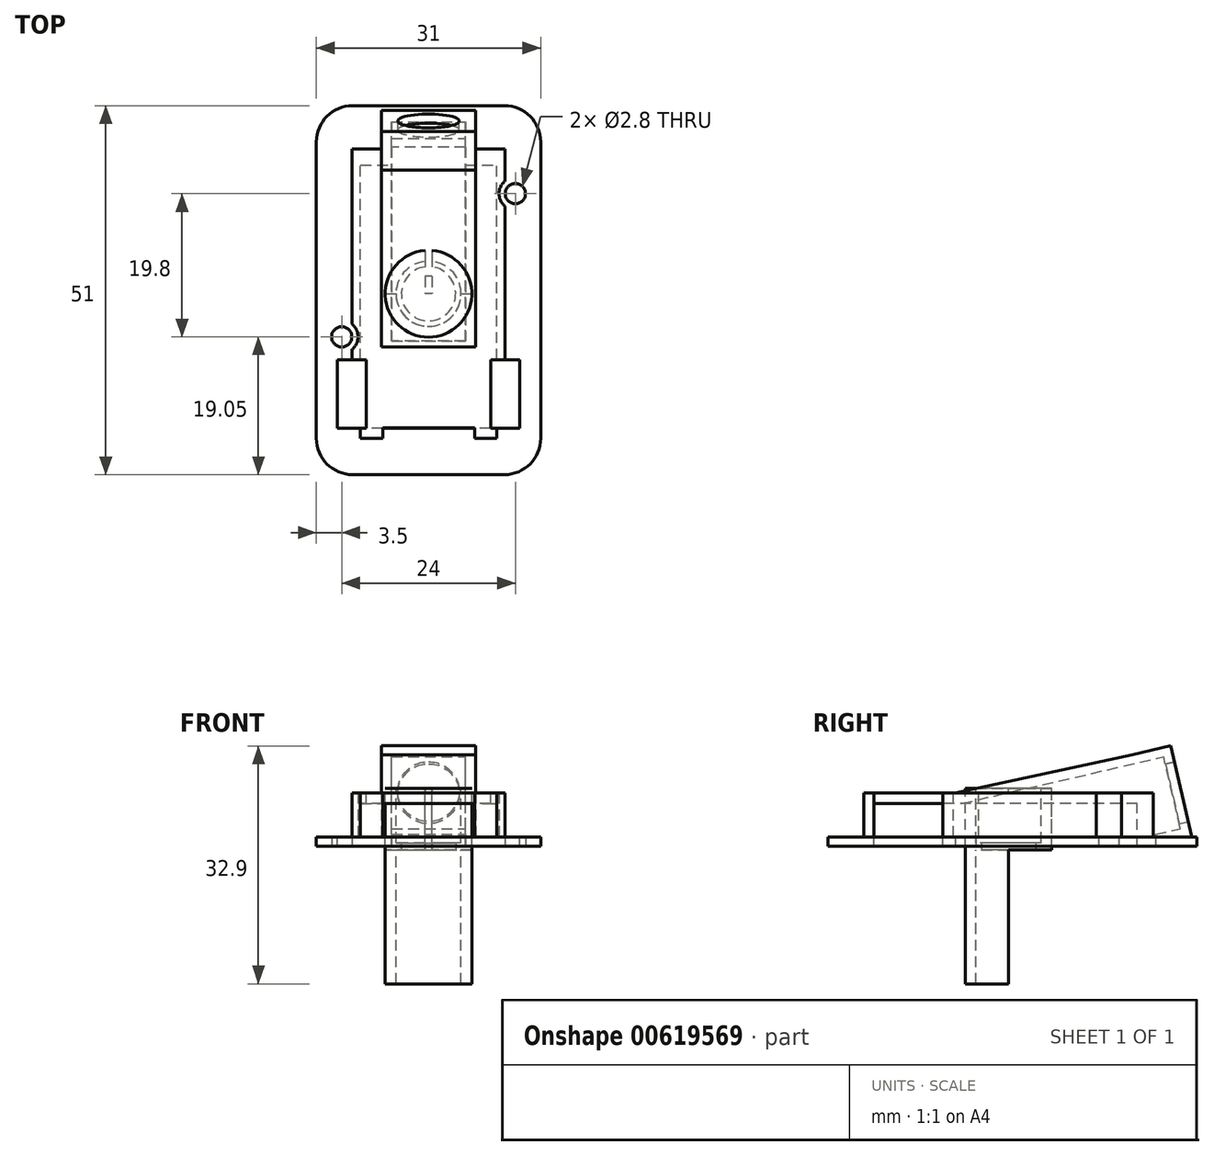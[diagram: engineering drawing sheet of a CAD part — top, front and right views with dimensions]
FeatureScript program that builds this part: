
annotation { "Feature Type Name" : "Feature", "Feature Type Description" : "" }
export const myFeature = defineFeature(function(context is Context, id is Id, definition is map)
    precondition{}
    {
        {
            var Q0;
            Q0=qCreatedBy(makeId("Top.planeOp"),FACE);
            var sketch = newSketch(context, id + "F0", { "sketchPlane" : qUnion([Q0])});
            skLineSegment(sketch, "E0.bottom", {"start": v(-15.5, 20) * mm, "end": v(15.5, 20) * mm});
            skLineSegment(sketch, "E0.top", {"start": v(-15.5, -20) * mm, "end": v(15.5, -20) * mm});
            skLineSegment(sketch, "E0.left", {"start": v(-15.5, 20) * mm, "end": v(-15.5, -20) * mm});
            skLineSegment(sketch, "E0.right", {"start": v(15.5, 20) * mm, "end": v(15.5, -20) * mm});
            skCircle(sketch, "E1", {"center": v(-12, -5.95) * mm, "radius": 1.4 * mm});
            skCircle(sketch, "E2", {"center": v(12, 13.85) * mm, "radius": 1.4 * mm});
            skLineSegment(sketch, "E3", {"start": v(-12, -5.95) * mm, "end": v(12, 13.85) * mm, "construction": true});
            skSolve(sketch);
        }
        {
            var Q0;
            Q0=makeQuery(id+"F0.imprint","IMPRINT",FACE,{"disambiguationData":[TD([[makeQuery(id+"F0.imprint","IMPRINT",EDGE,{"derivedFrom":sQuery(id+"F0.wireOp",EDGE,"E0.bottom")}),-1.0]])]});
            extrude(context, id + "F1", {"entities" : qUnion([Q0]), "depth" : 1.3 * mm, "offsetDistance" : 25 * mm});
        }
        {
            var Q0;
            Q0=makeQuery(id+"F1.opExtrude","CAP_FACE",FACE,{"disambiguationData":[OSD([sQuery(id+"F0.wireOp",EDGE,"E0.bottom"),sQuery(id+"F0.wireOp",EDGE,"E0.top"),sQuery(id+"F0.wireOp",EDGE,"E0.left"),sQuery(id+"F0.wireOp",EDGE,"E0.right"),sQuery(id+"F0.wireOp",EDGE,"E1"),sQuery(id+"F0.wireOp",EDGE,"E2")])],"isStart":true});
            var sketch = newSketch(context, id + "F2", { "sketchPlane" : qUnion([Q0])});
            skSolve(sketch);
        }
        {
            var Q0;
            Q0=qCreatedBy(makeId("Top.planeOp"),FACE);
            var sketch = newSketch(context, id + "F3", { "sketchPlane" : qUnion([Q0])});
            skLineSegment(sketch, "E4.bottom", {"start": v(9.1, 16) * mm, "end": v(-9.1, 16) * mm});
            skLineSegment(sketch, "E4.top", {"start": v(9.1, -20) * mm, "end": v(-9.1, -20) * mm});
            skLineSegment(sketch, "E4.left", {"start": v(9.1, 16) * mm, "end": v(9.1, -20) * mm});
            skLineSegment(sketch, "E4.right", {"start": v(-9.1, 16) * mm, "end": v(-9.1, -20) * mm});
            skSolve(sketch);
        }
        {
            var Q0;
            Q0=makeQuery(id+"F1.opExtrude","CAP_FACE",FACE,{"disambiguationData":[OSD([sQuery(id+"F0.wireOp",EDGE,"E0.bottom"),sQuery(id+"F0.wireOp",EDGE,"E0.top"),sQuery(id+"F0.wireOp",EDGE,"E0.left"),sQuery(id+"F0.wireOp",EDGE,"E0.right"),sQuery(id+"F0.wireOp",EDGE,"E1"),sQuery(id+"F0.wireOp",EDGE,"E2")])],"isStart":false});
            var sketch = newSketch(context, id + "F4", { "sketchPlane" : qUnion([Q0])});
            skCircle(sketch, "E5", {"center": v(0, 4.35) * mm, "radius": 4.15 * mm});
            skSolve(sketch);
        }
        {
            var Q0;
            Q0 = qSketchRegion(id + "F4", true);
            extrude(context, id + "F5", {"entities" : qUnion([Q0]), "operationType" : NewBodyOperationType.REMOVE, "endBound" : BoundingType.SYMMETRIC, "oppositeDirection" : true, "depth" : 25 * mm, "offsetDistance" : 25 * mm});
        }
        {
            var Q0;
            Q0=makeQuery(id+"F2.imprint","IMPRINT",FACE,{"disambiguationData":[TD([[makeQuery(id+"F2.imprint","IMPRINT",EDGE,{"derivedFrom":makeQuery(id+"F1.opExtrude","CAP_EDGE",EDGE,{"disambiguationData":[OSD([sQuery(id+"F0.wireOp",EDGE,"E0.bottom")])],"isStart":true})}),1.0]])]});
            var sketch = newSketch(context, id + "F6", { "sketchPlane" : qUnion([Q0])});
            skLineSegment(sketch, "E6.bottom", {"start": v(9.4, -16.3) * mm, "end": v(-9.4, -16.3) * mm});
            skLineSegment(sketch, "E6.left", {"start": v(9.4, -16.3) * mm, "end": v(9.4, 20) * mm});
            skLineSegment(sketch, "E6.right", {"start": v(-9.4, -16.3) * mm, "end": v(-9.4, 20) * mm});
            skLineSegment(sketch, "E7", {"start": v(9.4, 20) * mm, "end": v(10.6, 20) * mm});
            skLineSegment(sketch, "E8", {"start": v(10.6, 20) * mm, "end": v(10.6, -20) * mm});
            skLineSegment(sketch, "E9", {"start": v(10.6, -20) * mm, "end": v(0, -20) * mm});
            skLineSegment(sketch, "E10.MirrorCS", {"start": v(-9.4, 20) * mm, "end": v(-10.6, 20) * mm});
            skLineSegment(sketch, "E11.MirrorCS", {"start": v(-10.6, -20) * mm, "end": v(0, -20) * mm});
            skLineSegment(sketch, "E12.MirrorCS", {"start": v(-10.6, 20) * mm, "end": v(-10.6, -20) * mm});
            skSolve(sketch);
        }
        {
            var Q0;
            Q0 = qSketchRegion(id + "F6", true);
            extrude(context, id + "F7", {"entities" : qUnion([Q0]), "operationType" : NewBodyOperationType.ADD, "oppositeDirection" : true, "depth" : 5.9 * mm, "offsetDistance" : 25 * mm});
        }
        {
            var Q0;
            Q0=makeQuery(id+"F7.opExtrude","CAP_FACE",FACE,{"disambiguationData":[OSD([sQuery(id+"F6.wireOp",EDGE,"E6.bottom"),sQuery(id+"F6.wireOp",EDGE,"E6.left"),sQuery(id+"F6.wireOp",EDGE,"E6.right"),sQuery(id+"F6.wireOp",EDGE,"E7"),sQuery(id+"F6.wireOp",EDGE,"E8"),sQuery(id+"F6.wireOp",EDGE,"E9"),sQuery(id+"F6.wireOp",EDGE,"E10.MirrorCS"),sQuery(id+"F6.wireOp",EDGE,"E11.MirrorCS"),sQuery(id+"F6.wireOp",EDGE,"E12.MirrorCS")])],"isStart":false});
            var sketch = newSketch(context, id + "F8", { "sketchPlane" : qUnion([Q0])});
            skLineSegment(sketch, "E13.bottom", {"start": v(-10.6, 20) * mm, "end": v(10.6, 20) * mm});
            skLineSegment(sketch, "E13.top", {"start": v(-10.6, -20) * mm, "end": v(10.6, -20) * mm});
            skLineSegment(sketch, "E13.left", {"start": v(-10.6, 20) * mm, "end": v(-10.6, -20) * mm});
            skLineSegment(sketch, "E13.right", {"start": v(10.6, 20) * mm, "end": v(10.6, -20) * mm});
            skSolve(sketch);
        }
        {
            var Q0;
            Q0 = qSketchRegion(id + "F8", true);
            extrude(context, id + "F9", {"entities" : qUnion([Q0]), "operationType" : NewBodyOperationType.ADD, "depth" : 1.5 * mm, "offsetDistance" : 25 * mm});
        }
        {
            var Q0;
            {var subQ0=sQuery(id+"F0.wireOp",EDGE,"E0.top");Q0=makeQuery(id+"F7.boolean.opBoolean","SPLIT",FACE,{"disambiguationData":[TD([makeQuery(id+"F5.boolean.opBoolean","COPY",FACE,{"derivedFrom":makeQuery(id+"F5.opExtrude","SWEPT_FACE",FACE,{"disambiguationData":[OSD([sQuery(id+"F4.wireOp",EDGE,"E5")])]})})])],"derivedFrom":makeQuery(id+"F1.opExtrude","CAP_FACE",FACE,{"disambiguationData":[OSD([sQuery(id+"F0.wireOp",EDGE,"E0.bottom"),subQ0,sQuery(id+"F0.wireOp",EDGE,"E0.left"),sQuery(id+"F0.wireOp",EDGE,"E0.right"),sQuery(id+"F0.wireOp",EDGE,"E1"),sQuery(id+"F0.wireOp",EDGE,"E2")])],"isStart":false})});}
            extrude(context, id + "F10", {"entities" : qUnion([Q0]), "operationType" : NewBodyOperationType.REMOVE, "oppositeDirection" : true, "depth" : 25 * mm, "offsetDistance" : 25 * mm});
        }
        {
            var Q0;
            Q0=makeQuery(id+"F9.opExtrude","CAP_FACE",FACE,{"disambiguationData":[OSD([sQuery(id+"F8.wireOp",EDGE,"E13.bottom"),sQuery(id+"F8.wireOp",EDGE,"E13.top"),sQuery(id+"F8.wireOp",EDGE,"E13.left"),sQuery(id+"F8.wireOp",EDGE,"E13.right"),sQuery(id+"F8.wireOp",EDGE,"e1htHEVN-ULea-oUP2-wwqg-xbvDfwhMSIQY")])],"isStart":false});
            var sketch = newSketch(context, id + "F11", { "sketchPlane" : qUnion([Q0])});
            skLineSegment(sketch, "E14.bottom", {"start": v(10.6, -20.5) * mm, "end": v(8.6, -20.5) * mm});
            skLineSegment(sketch, "E14.top", {"start": v(10.6, -11.5) * mm, "end": v(8.6, -11.5) * mm});
            skLineSegment(sketch, "E14.left", {"start": v(10.6, -20.5) * mm, "end": v(10.6, -11.5) * mm});
            skLineSegment(sketch, "E14.right", {"start": v(8.6, -20.5) * mm, "end": v(8.6, -11.5) * mm});
            skLineSegment(sketch, "E15.MirrorCS", {"start": v(-10.6, -20.5) * mm, "end": v(-8.6, -20.5) * mm});
            skLineSegment(sketch, "E16.MirrorCS", {"start": v(-10.6, -11.5) * mm, "end": v(-8.6, -11.5) * mm});
            skLineSegment(sketch, "E17.MirrorCS", {"start": v(-8.6, -20.5) * mm, "end": v(-8.6, -11.5) * mm});
            skLineSegment(sketch, "E18.MirrorCS", {"start": v(-10.6, -20.5) * mm, "end": v(-10.6, -11.5) * mm});
            skSolve(sketch);
        }
        {
            var Q0;
            Q0 = qSketchRegion(id + "F11", true);
            var Q1;
            {var subQ0=sQuery(id+"F0.wireOp",EDGE,"E2");var subQ1=sQuery(id+"F0.wireOp",EDGE,"E0.top");var subQ2=sQuery(id+"F0.wireOp",EDGE,"E0.right");var subQ3=sQuery(id+"F0.wireOp",EDGE,"E0.bottom");Q1=makeQuery(id+"F7.boolean.opBoolean","SPLIT",FACE,{"disambiguationData":[TD([makeQuery(id+"F1.opExtrude","SWEPT_FACE",FACE,{"disambiguationData":[OSD([subQ2])]})])],"derivedFrom":makeQuery(id+"F1.opExtrude","CAP_FACE",FACE,{"disambiguationData":[OSD([subQ3,subQ1,sQuery(id+"F0.wireOp",EDGE,"E0.left"),subQ2,sQuery(id+"F0.wireOp",EDGE,"E1"),subQ0])],"isStart":false})});}
            extrude(context, id + "F12", {"entities" : qUnion([Q0]), "operationType" : NewBodyOperationType.REMOVE, "endBound" : BoundingType.UP_TO_SURFACE, "oppositeDirection" : true, "depth" : 6.7 * mm, "endBoundEntityFace" : qUnion([Q1]), "offsetDistance" : 25 * mm});
        }
        {
            var Q0;
            Q0=makeQuery(id+"F2.imprint","IMPRINT",FACE,{"disambiguationData":[TD([[makeQuery(id+"F2.imprint","IMPRINT",EDGE,{"derivedFrom":makeQuery(id+"F1.opExtrude","CAP_EDGE",EDGE,{"disambiguationData":[OSD([sQuery(id+"F0.wireOp",EDGE,"E0.bottom")])],"isStart":true})}),1.0]])]});
            var sketch = newSketch(context, id + "F13", { "sketchPlane" : qUnion([Q0])});
            skLineSegment(sketch, "E19.bottom", {"start": v(9.4, 20) * mm, "end": v(-9.4, 20) * mm});
            skLineSegment(sketch, "E19.top", {"start": v(9.4, 18.6) * mm, "end": v(-9.4, 18.6) * mm});
            skLineSegment(sketch, "E19.left", {"start": v(-9.4, 18.6) * mm, "end": v(-9.4, 20) * mm});
            skLineSegment(sketch, "E19.right", {"start": v(9.4, 18.6) * mm, "end": v(9.4, 20) * mm});
            skSolve(sketch);
        }
        {
            var Q0;
            Q0 = qSketchRegion(id + "F13", true);
            var Q1;
            Q1=makeQuery(id+"F9.opExtrude","CAP_FACE",FACE,{"disambiguationData":[OSD([sQuery(id+"F8.wireOp",EDGE,"E13.bottom"),sQuery(id+"F8.wireOp",EDGE,"E13.top"),sQuery(id+"F8.wireOp",EDGE,"E13.left"),sQuery(id+"F8.wireOp",EDGE,"E13.right"),sQuery(id+"F8.wireOp",EDGE,"e1htHEVN-ULea-oUP2-wwqg-xbvDfwhMSIQY")])],"isStart":true});
            extrude(context, id + "F14", {"entities" : qUnion([Q0]), "operationType" : NewBodyOperationType.ADD, "endBound" : BoundingType.UP_TO_SURFACE, "oppositeDirection" : true, "depth" : 25 * mm, "endBoundEntityFace" : qUnion([Q1]), "offsetDistance" : 25 * mm});
        }
        {
            var Q0;
            Q0=qCreatedBy(makeId("Right.planeOp"),FACE);
            var sketch = newSketch(context, id + "F15", { "sketchPlane" : qUnion([Q0])});
            skLineSegment(sketch, "E20", {"start": v(20, 0) * mm, "end": v(25.36, 1.24) * mm});
            skLineSegment(sketch, "E21", {"start": v(25.36, 1.24) * mm, "end": v(22.43, 13.9) * mm});
            skLineSegment(sketch, "E22", {"start": v(22.43, 13.9) * mm, "end": v(17.08, 12.67) * mm});
            skLineSegment(sketch, "E23", {"start": v(17.08, 12.67) * mm, "end": v(20, 0) * mm});
            skSolve(sketch);
        }
        {
            var Q0;
            Q0=makeQuery(id+"F15.imprint","IMPRINT",FACE,{"disambiguationData":[TD([[makeQuery(id+"F15.imprint","IMPRINT",EDGE,{"derivedFrom":sQuery(id+"F15.wireOp",EDGE,"E20")}),1.0]])]});
            extrude(context, id + "F16", {"entities" : qUnion([Q0]), "operationType" : NewBodyOperationType.ADD, "endBound" : BoundingType.SYMMETRIC, "depth" : 13 * mm, "offsetDistance" : 25 * mm});
        }
        {
            var Q0;
            Q0=qCreatedBy(makeId("Right.planeOp"),FACE);
            var sketch = newSketch(context, id + "F17", { "sketchPlane" : qUnion([Q0])});
            skLineSegment(sketch, "E24", {"start": v(17.08, 12.67) * mm, "end": v(-7.36, 7.4) * mm});
            skLineSegment(sketch, "E25", {"start": v(-7.36, 7.4) * mm, "end": v(18.3, 7.4) * mm});
            skLineSegment(sketch, "E26", {"start": v(18.3, 7.4) * mm, "end": v(17.08, 12.67) * mm});
            skSolve(sketch);
        }
        {
            var Q0;
            Q0 = qSketchRegion(id + "F17", true);
            extrude(context, id + "F18", {"entities" : qUnion([Q0]), "operationType" : NewBodyOperationType.ADD, "endBound" : BoundingType.SYMMETRIC, "depth" : 13 * mm, "offsetDistance" : 25 * mm});
        }
        {
            var Q0;
            Q0=makeQuery(id+"F16.opExtrude","SWEPT_FACE",FACE,{"disambiguationData":[OSD([sQuery(id+"F15.wireOp",EDGE,"E21")])]});
            var sketch = newSketch(context, id + "F19", { "sketchPlane" : qUnion([Q0])});
            skCircle(sketch, "E27", {"center": v(0, 2) * mm, "radius": 4.25 * mm});
            skSolve(sketch);
        }
        {
            var Q0;
            Q0=makeQuery(id+"F19.imprint","IMPRINT",FACE,{"disambiguationData":[TD([[makeQuery(id+"F19.imprint","IMPRINT",EDGE,{"derivedFrom":sQuery(id+"F19.wireOp",EDGE,"E27")}),1.0]])]});
            extrude(context, id + "F20", {"entities" : qUnion([Q0]), "operationType" : NewBodyOperationType.REMOVE, "oppositeDirection" : true, "depth" : 25 * mm, "offsetDistance" : 25 * mm});
        }
        {
            var Q0;
            Q0=makeQuery(id+"F16.opExtrude","SWEPT_FACE",FACE,{"disambiguationData":[OSD([sQuery(id+"F15.wireOp",EDGE,"E21")])]});
            var sketch = newSketch(context, id + "F21", { "sketchPlane" : qUnion([Q0])});
            skLineSegment(sketch, "E28.bottom", {"start": v(5.1, -2.95) * mm, "end": v(-5.1, -2.95) * mm});
            skLineSegment(sketch, "E28.top", {"start": v(5.1, 7.25) * mm, "end": v(-5.1, 7.25) * mm});
            skLineSegment(sketch, "E28.left", {"start": v(5.1, -2.95) * mm, "end": v(5.1, 7.25) * mm});
            skLineSegment(sketch, "E28.right", {"start": v(-5.1, -2.95) * mm, "end": v(-5.1, 7.25) * mm});
            skSolve(sketch);
        }
        {
            var Q0;
            Q0 = qSketchRegion(id + "F21", true);
            extrude(context, id + "F22", {"entities" : qUnion([Q0]), "operationType" : NewBodyOperationType.REMOVE, "oppositeDirection" : true, "depth" : 30 * mm, "offsetDistance" : 25 * mm, "hasSecondDirection" : true, "secondDirectionOppositeDirection" : true, "secondDirectionDepth" : 1.3 * mm});
        }
        {
            var Q0;
            Q0=makeQuery(id+"F2.imprint","IMPRINT",FACE,{"disambiguationData":[TD([[makeQuery(id+"F2.imprint","IMPRINT",EDGE,{"derivedFrom":makeQuery(id+"F1.opExtrude","CAP_EDGE",EDGE,{"disambiguationData":[OSD([sQuery(id+"F0.wireOp",EDGE,"E0.bottom")])],"isStart":true})}),1.0]])]});
            var sketch = newSketch(context, id + "F23", { "sketchPlane" : qUnion([Q0])});
            skLineSegment(sketch, "E29.bottom", {"start": v(-15.5, -20) * mm, "end": v(15.5, -20) * mm});
            skLineSegment(sketch, "E29.top", {"start": v(-15.5, -26) * mm, "end": v(15.5, -26) * mm});
            skLineSegment(sketch, "E29.left", {"start": v(-15.5, -20) * mm, "end": v(-15.5, -26) * mm});
            skLineSegment(sketch, "E29.right", {"start": v(15.5, -20) * mm, "end": v(15.5, -26) * mm});
            skLineSegment(sketch, "E30.bottom", {"start": v(15.5, 20) * mm, "end": v(-15.5, 20) * mm});
            skLineSegment(sketch, "E30.top", {"start": v(15.5, 25) * mm, "end": v(-15.5, 25) * mm});
            skLineSegment(sketch, "E30.left", {"start": v(15.5, 20) * mm, "end": v(15.5, 25) * mm});
            skLineSegment(sketch, "E30.right", {"start": v(-15.5, 20) * mm, "end": v(-15.5, 25) * mm});
            skSolve(sketch);
        }
        {
            var Q0;
            Q0 = qSketchRegion(id + "F23", true);
            extrude(context, id + "F24", {"entities" : qUnion([Q0]), "operationType" : NewBodyOperationType.ADD, "oppositeDirection" : true, "depth" : 1.3 * mm, "offsetDistance" : 25 * mm});
        }
        {
            var Q0;
            Q0=makeQuery(id+"F16.opExtrude","SWEPT_FACE",FACE,{"disambiguationData":[OSD([sQuery(id+"F15.wireOp",EDGE,"E21")])]});
            var sketch = newSketch(context, id + "F25", { "sketchPlane" : qUnion([Q0])});
            skLineSegment(sketch, "E31.bottom", {"start": v(4.25, -2.25) * mm, "end": v(-4.25, -2.25) * mm});
            skLineSegment(sketch, "E31.top", {"start": v(4.25, 6.25) * mm, "end": v(-4.25, 6.25) * mm});
            skLineSegment(sketch, "E31.left", {"start": v(4.25, -2.25) * mm, "end": v(4.25, 6.25) * mm});
            skLineSegment(sketch, "E31.right", {"start": v(-4.25, -2.25) * mm, "end": v(-4.25, 6.25) * mm});
            skSolve(sketch);
        }
        {
            var Q0;
            Q0 = qSketchRegion(id + "F25", true);
            extrude(context, id + "F26", {"entities" : qUnion([Q0]), "operationType" : NewBodyOperationType.REMOVE, "oppositeDirection" : true, "depth" : 35 * mm, "offsetDistance" : 25 * mm, "hasSecondDirection" : true, "secondDirectionOppositeDirection" : true, "secondDirectionDepth" : 1.3 * mm});
        }
        {
            var Q0;
            Q0=makeQuery(id+"F24.opExtrude","SWEPT_EDGE",EDGE,{"disambiguationData":[OSD([sQuery(id+"F23.wireOp",EDGE,"E29.top"),sQuery(id+"F23.wireOp",EDGE,"E29.left")])]});
            var Q1;
            Q1=makeQuery(id+"F24.opExtrude","SWEPT_EDGE",EDGE,{"disambiguationData":[OSD([sQuery(id+"F23.wireOp",EDGE,"E29.top"),sQuery(id+"F23.wireOp",EDGE,"E29.right")])]});
            var Q2;
            Q2=makeQuery(id+"F24.opExtrude","SWEPT_EDGE",EDGE,{"disambiguationData":[OSD([sQuery(id+"F23.wireOp",EDGE,"E30.top"),sQuery(id+"F23.wireOp",EDGE,"E30.left")])]});
            var Q3;
            Q3=makeQuery(id+"F24.opExtrude","SWEPT_EDGE",EDGE,{"disambiguationData":[OSD([sQuery(id+"F23.wireOp",EDGE,"E30.top"),sQuery(id+"F23.wireOp",EDGE,"E30.right")])]});
            fillet(context, id + "F27", {"entities" : qUnion([Q0, Q1, Q2, Q3]), "radius" : 5 * mm, "tangentPropagation" : true, "allowEdgeOverflow" : false});
        }
        {
            var Q0;
            Q0=makeQuery(id+"F9.opExtrude","CAP_FACE",FACE,{"disambiguationData":[OSD([sQuery(id+"F8.wireOp",EDGE,"E13.bottom"),sQuery(id+"F8.wireOp",EDGE,"E13.top"),sQuery(id+"F8.wireOp",EDGE,"E13.left"),sQuery(id+"F8.wireOp",EDGE,"E13.right")])],"isStart":false});
            var sketch = newSketch(context, id + "F28", { "sketchPlane" : qUnion([Q0])});
            skLineSegment(sketch, "E32.bottom", {"start": v(6.35, -29.94) * mm, "end": v(-6.35, -29.94) * mm});
            skLineSegment(sketch, "E32.top", {"start": v(6.35, -18.5) * mm, "end": v(-6.35, -18.5) * mm});
            skLineSegment(sketch, "E32.left", {"start": v(6.35, -29.94) * mm, "end": v(6.35, -18.5) * mm});
            skLineSegment(sketch, "E32.right", {"start": v(-6.35, -29.94) * mm, "end": v(-6.35, -18.5) * mm});
            skSolve(sketch);
        }
        {
            var Q0;
            Q0 = qSketchRegion(id + "F28", true);
            var Q1;
            {var subQ0=sQuery(id+"F0.wireOp",EDGE,"E1");var subQ1=sQuery(id+"F0.wireOp",EDGE,"E0.left");var subQ2=sQuery(id+"F0.wireOp",EDGE,"E0.top");var subQ4=sQuery(id+"F0.wireOp",EDGE,"E0.bottom");var subQ9=sQuery(id+"F0.wireOp",EDGE,"E2");var subQ10=sQuery(id+"F0.wireOp",EDGE,"E0.right");var subQ11=makeQuery(id+"F1.opExtrude","CAP_FACE",FACE,{"disambiguationData":[OSD([subQ4,subQ2,subQ1,subQ10,subQ0,subQ9])],"isStart":false});Q1=makeQuery(id+"F24.boolean.opBoolean","MERGE",FACE,{"derivedFrom":[makeQuery(id+"F7.boolean.opBoolean","SPLIT",FACE,{"disambiguationData":[TD([makeQuery(id+"F1.opExtrude","SWEPT_FACE",FACE,{"disambiguationData":[OSD([subQ10])]})])],"derivedFrom":subQ11}),makeQuery(id+"F12.boolean.opBoolean","MERGE",FACE,{"derivedFrom":[makeQuery(id+"F7.boolean.opBoolean","SPLIT",FACE,{"disambiguationData":[TD([makeQuery(id+"F1.opExtrude","SWEPT_FACE",FACE,{"disambiguationData":[OSD([subQ1])]})])],"derivedFrom":subQ11}),makeQuery(id+"F12.opExtrude","CAP_FACE",FACE,{"disambiguationData":[OSD([sQuery(id+"F11.wireOp",EDGE,"E15.MirrorCS"),sQuery(id+"F11.wireOp",EDGE,"E16.MirrorCS"),sQuery(id+"F11.wireOp",EDGE,"E17.MirrorCS"),sQuery(id+"F11.wireOp",EDGE,"E18.MirrorCS")])],"isStart":false})]}),makeQuery(id+"F24.opExtrude","CAP_FACE",FACE,{"disambiguationData":[OSD([sQuery(id+"F23.wireOp",EDGE,"E29.bottom"),sQuery(id+"F23.wireOp",EDGE,"E29.top"),sQuery(id+"F23.wireOp",EDGE,"E29.left"),sQuery(id+"F23.wireOp",EDGE,"E29.right")])],"isStart":false}),makeQuery(id+"F24.opExtrude","CAP_FACE",FACE,{"disambiguationData":[OSD([sQuery(id+"F23.wireOp",EDGE,"E30.bottom"),sQuery(id+"F23.wireOp",EDGE,"E30.top"),sQuery(id+"F23.wireOp",EDGE,"E30.left"),sQuery(id+"F23.wireOp",EDGE,"E30.right")])],"isStart":false})]});}
            extrude(context, id + "F29", {"entities" : qUnion([Q0]), "operationType" : NewBodyOperationType.REMOVE, "endBound" : BoundingType.UP_TO_SURFACE, "oppositeDirection" : true, "depth" : 25 * mm, "endBoundEntityFace" : qUnion([Q1]), "offsetDistance" : 25 * mm});
        }
        {
            var Q0;
            Q0=makeQuery(id+"F24.boolean.opBoolean","MERGE",FACE,{"derivedFrom":[makeQuery(id+"F14.boolean.opBoolean","MERGE",FACE,{"derivedFrom":[makeQuery(id+"F1.opExtrude","CAP_FACE",FACE,{"disambiguationData":[OSD([sQuery(id+"F0.wireOp",EDGE,"E0.bottom"),sQuery(id+"F0.wireOp",EDGE,"E0.top"),sQuery(id+"F0.wireOp",EDGE,"E0.left"),sQuery(id+"F0.wireOp",EDGE,"E0.right"),sQuery(id+"F0.wireOp",EDGE,"E1"),sQuery(id+"F0.wireOp",EDGE,"E2")])],"isStart":true}),makeQuery(id+"F14.opExtrude","CAP_FACE",FACE,{"disambiguationData":[OSD([sQuery(id+"F13.wireOp",EDGE,"E19.bottom"),sQuery(id+"F13.wireOp",EDGE,"E19.top"),sQuery(id+"F13.wireOp",EDGE,"E19.left"),sQuery(id+"F13.wireOp",EDGE,"E19.right")])],"isStart":true})]}),makeQuery(id+"F24.opExtrude","CAP_FACE",FACE,{"disambiguationData":[OSD([sQuery(id+"F23.wireOp",EDGE,"E29.bottom"),sQuery(id+"F23.wireOp",EDGE,"E29.top"),sQuery(id+"F23.wireOp",EDGE,"E29.left"),sQuery(id+"F23.wireOp",EDGE,"E29.right")])],"isStart":true}),makeQuery(id+"F24.opExtrude","CAP_FACE",FACE,{"disambiguationData":[OSD([sQuery(id+"F23.wireOp",EDGE,"E30.bottom"),sQuery(id+"F23.wireOp",EDGE,"E30.top"),sQuery(id+"F23.wireOp",EDGE,"E30.left"),sQuery(id+"F23.wireOp",EDGE,"E30.right")])],"isStart":true})]});
            var sketch = newSketch(context, id + "F30", { "sketchPlane" : qUnion([Q0])});
            skLineSegment(sketch, "E33.bottom", {"start": v(5.1, -20.3) * mm, "end": v(-5.1, -20.3) * mm});
            skLineSegment(sketch, "E33.top", {"start": v(5.1, -14.26) * mm, "end": v(-5.1, -14.26) * mm});
            skLineSegment(sketch, "E33.left", {"start": v(5.1, -20.3) * mm, "end": v(5.1, -14.26) * mm});
            skLineSegment(sketch, "E33.right", {"start": v(-5.1, -20.3) * mm, "end": v(-5.1, -14.26) * mm});
            skSolve(sketch);
        }
        {
            var Q0;
            Q0 = qSketchRegion(id + "F30", true);
            extrude(context, id + "F31", {"entities" : qUnion([Q0]), "operationType" : NewBodyOperationType.REMOVE, "oppositeDirection" : true, "depth" : 2 * mm, "offsetDistance" : 25 * mm});
        }
        {
            var Q0;
            {var subQ0=sQuery(id+"F23.wireOp",EDGE,"E30.right");var subQ1=sQuery(id+"F23.wireOp",EDGE,"E30.left");var subQ2=sQuery(id+"F23.wireOp",EDGE,"E30.top");var subQ3=sQuery(id+"F23.wireOp",EDGE,"E30.bottom");var subQ4=sQuery(id+"F23.wireOp",EDGE,"E29.right");var subQ5=sQuery(id+"F23.wireOp",EDGE,"E29.left");var subQ6=sQuery(id+"F23.wireOp",EDGE,"E29.top");var subQ7=sQuery(id+"F23.wireOp",EDGE,"E29.bottom");var subQ8=sQuery(id+"F11.wireOp",EDGE,"E18.MirrorCS");var subQ9=sQuery(id+"F11.wireOp",EDGE,"E17.MirrorCS");var subQ10=sQuery(id+"F11.wireOp",EDGE,"E16.MirrorCS");var subQ11=sQuery(id+"F11.wireOp",EDGE,"E15.MirrorCS");var subQ12=sQuery(id+"F11.wireOp",EDGE,"E14.right");var subQ13=sQuery(id+"F11.wireOp",EDGE,"E14.left");var subQ14=sQuery(id+"F11.wireOp",EDGE,"E14.top");var subQ15=sQuery(id+"F11.wireOp",EDGE,"E14.bottom");var subQ16=sQuery(id+"F0.wireOp",EDGE,"E2");var subQ17=sQuery(id+"F0.wireOp",EDGE,"E1");var subQ18=sQuery(id+"F0.wireOp",EDGE,"E0.right");var subQ19=sQuery(id+"F0.wireOp",EDGE,"E0.left");var subQ20=sQuery(id+"F0.wireOp",EDGE,"E0.top");var subQ21=sQuery(id+"F0.wireOp",EDGE,"E0.bottom");var subQ27=makeQuery(id+"F1.opExtrude","CAP_FACE",FACE,{"disambiguationData":[OSD([subQ21,subQ20,subQ19,subQ18,subQ17,subQ16])],"isStart":false});Q0=makeQuery(id+"F29.boolean.opBoolean","MERGE",FACE,{"derivedFrom":[makeQuery(id+"F24.boolean.opBoolean","MERGE",FACE,{"derivedFrom":[makeQuery(id+"F12.boolean.opBoolean","MERGE",FACE,{"derivedFrom":[makeQuery(id+"F7.boolean.opBoolean","SPLIT",FACE,{"disambiguationData":[TD([makeQuery(id+"F1.opExtrude","SWEPT_FACE",FACE,{"disambiguationData":[OSD([subQ19])]})])],"derivedFrom":subQ27}),makeQuery(id+"F12.opExtrude","CAP_FACE",FACE,{"disambiguationData":[OSD([subQ11,subQ10,subQ9,subQ8])],"isStart":false})]}),makeQuery(id+"F12.boolean.opBoolean","MERGE",FACE,{"derivedFrom":[makeQuery(id+"F7.boolean.opBoolean","SPLIT",FACE,{"disambiguationData":[TD([makeQuery(id+"F1.opExtrude","SWEPT_FACE",FACE,{"disambiguationData":[OSD([subQ18])]})])],"derivedFrom":subQ27}),makeQuery(id+"F12.opExtrude","CAP_FACE",FACE,{"disambiguationData":[OSD([subQ15,subQ14,subQ13,subQ12])],"isStart":false})]}),makeQuery(id+"F24.opExtrude","CAP_FACE",FACE,{"disambiguationData":[OSD([subQ7,subQ6,subQ5,subQ4])],"isStart":false}),makeQuery(id+"F24.opExtrude","CAP_FACE",FACE,{"disambiguationData":[OSD([subQ3,subQ2,subQ1,subQ0])],"isStart":false})]}),makeQuery(id+"F29.opExtrude","CAP_FACE",FACE,{"disambiguationData":[OSD([subQ21,subQ20,subQ19,subQ18,subQ17,subQ16,subQ15,subQ14,subQ13,subQ12,subQ11,subQ10,subQ9,subQ8,subQ7,subQ6,subQ5,subQ4,subQ3,subQ2,subQ1,subQ0])],"isStart":false})]});}
            var sketch = newSketch(context, id + "F32", { "sketchPlane" : qUnion([Q0])});
            skCircle(sketch, "E34", {"center": v(-12, -5.95) * mm, "radius": 2.25 * mm});
            skCircle(sketch, "E35", {"center": v(12, 13.85) * mm, "radius": 2.25 * mm});
            skSolve(sketch);
        }
        {
            var Q0;
            Q0 = qSketchRegion(id + "F32", true);
            extrude(context, id + "F33", {"entities" : qUnion([Q0]), "operationType" : NewBodyOperationType.REMOVE, "depth" : 25 * mm, "offsetDistance" : 25 * mm});
        }
        {
            var Q0;
            Q0=makeQuery(id+"F9.opExtrude","CAP_FACE",FACE,{"disambiguationData":[OSD([sQuery(id+"F8.wireOp",EDGE,"E13.bottom"),sQuery(id+"F8.wireOp",EDGE,"E13.top"),sQuery(id+"F8.wireOp",EDGE,"E13.left"),sQuery(id+"F8.wireOp",EDGE,"E13.right")])],"isStart":true});
            var sketch = newSketch(context, id + "F34", { "sketchPlane" : qUnion([Q0])});
            skLineSegment(sketch, "E36.bottom", {"start": v(-9.4, -16.3) * mm, "end": v(9.4, -16.3) * mm});
            skLineSegment(sketch, "E36.top", {"start": v(-9.4, -17.8) * mm, "end": v(9.4, -17.8) * mm});
            skLineSegment(sketch, "E36.left", {"start": v(-9.4, -16.3) * mm, "end": v(-9.4, -17.8) * mm});
            skLineSegment(sketch, "E36.right", {"start": v(9.4, -16.3) * mm, "end": v(9.4, -17.8) * mm});
            skSolve(sketch);
        }
        {
            var Q0;
            Q0 = qSketchRegion(id + "F34", true);
            extrude(context, id + "F35", {"entities" : qUnion([Q0]), "operationType" : NewBodyOperationType.REMOVE, "depth" : 25 * mm, "offsetDistance" : 25 * mm});
        }
        {
            var Q0;
            Q0=makeQuery(id+"F9.opExtrude","CAP_FACE",FACE,{"disambiguationData":[OSD([sQuery(id+"F8.wireOp",EDGE,"E13.bottom"),sQuery(id+"F8.wireOp",EDGE,"E13.top"),sQuery(id+"F8.wireOp",EDGE,"E13.left"),sQuery(id+"F8.wireOp",EDGE,"E13.right")])],"isStart":false});
            var sketch = newSketch(context, id + "F36", { "sketchPlane" : qUnion([Q0])});
            skLineSegment(sketch, "E37.bottom", {"start": v(8.6, -18.6) * mm, "end": v(12.6, -18.6) * mm});
            skLineSegment(sketch, "E37.top", {"start": v(8.6, -9.1) * mm, "end": v(12.6, -9.1) * mm});
            skLineSegment(sketch, "E37.left", {"start": v(8.6, -18.6) * mm, "end": v(8.6, -9.1) * mm});
            skLineSegment(sketch, "E37.right", {"start": v(12.6, -18.6) * mm, "end": v(12.6, -9.1) * mm});
            skLineSegment(sketch, "E38.MirrorCS", {"start": v(-8.6, -18.6) * mm, "end": v(-12.6, -18.6) * mm});
            skLineSegment(sketch, "E39.MirrorCS", {"start": v(-8.6, -18.6) * mm, "end": v(-8.6, -9.1) * mm});
            skLineSegment(sketch, "E40.MirrorCS", {"start": v(-12.6, -18.6) * mm, "end": v(-12.6, -9.1) * mm});
            skLineSegment(sketch, "E41.MirrorCS", {"start": v(-8.6, -9.1) * mm, "end": v(-12.6, -9.1) * mm});
            skSolve(sketch);
        }
        {
            var Q0;
            Q0 = qSketchRegion(id + "F36", true);
            extrude(context, id + "F37", {"entities" : qUnion([Q0]), "operationType" : NewBodyOperationType.REMOVE, "oppositeDirection" : true, "depth" : 25 * mm, "offsetDistance" : 25 * mm});
        }
        {
            var Q0;
            Q0=makeQuery(id+"F9.opExtrude","CAP_FACE",FACE,{"disambiguationData":[OSD([sQuery(id+"F8.wireOp",EDGE,"E13.bottom"),sQuery(id+"F8.wireOp",EDGE,"E13.top"),sQuery(id+"F8.wireOp",EDGE,"E13.left"),sQuery(id+"F8.wireOp",EDGE,"E13.right")])],"isStart":false});
            var sketch = newSketch(context, id + "F38", { "sketchPlane" : qUnion([Q0])});
            skLineSegment(sketch, "E42.bottom", {"start": v(-8.6, -20) * mm, "end": v(-9.4, -20) * mm});
            skLineSegment(sketch, "E42.top", {"start": v(-8.6, -18.6) * mm, "end": v(-9.4, -18.6) * mm});
            skLineSegment(sketch, "E42.left", {"start": v(-8.6, -20) * mm, "end": v(-8.6, -18.6) * mm});
            skLineSegment(sketch, "E42.right", {"start": v(-9.4, -20) * mm, "end": v(-9.4, -18.6) * mm});
            skLineSegment(sketch, "E43.MirrorCS", {"start": v(8.6, -18.6) * mm, "end": v(9.4, -18.6) * mm});
            skLineSegment(sketch, "E44.MirrorCS", {"start": v(8.6, -20) * mm, "end": v(9.4, -20) * mm});
            skLineSegment(sketch, "E45.MirrorCS", {"start": v(8.6, -20) * mm, "end": v(8.6, -18.6) * mm});
            skLineSegment(sketch, "E46.MirrorCS", {"start": v(9.4, -20) * mm, "end": v(9.4, -18.6) * mm});
            skSolve(sketch);
        }
        {
            var Q0;
            Q0 = qSketchRegion(id + "F38", true);
            var Q1;
            {var subQ0=sQuery(id+"F23.wireOp",EDGE,"E30.right");var subQ1=sQuery(id+"F23.wireOp",EDGE,"E30.left");var subQ2=sQuery(id+"F23.wireOp",EDGE,"E30.top");var subQ3=sQuery(id+"F23.wireOp",EDGE,"E30.bottom");var subQ4=sQuery(id+"F23.wireOp",EDGE,"E29.right");var subQ5=sQuery(id+"F23.wireOp",EDGE,"E29.left");var subQ6=sQuery(id+"F23.wireOp",EDGE,"E29.top");var subQ7=sQuery(id+"F23.wireOp",EDGE,"E29.bottom");var subQ8=sQuery(id+"F11.wireOp",EDGE,"E18.MirrorCS");var subQ9=sQuery(id+"F11.wireOp",EDGE,"E17.MirrorCS");var subQ10=sQuery(id+"F11.wireOp",EDGE,"E16.MirrorCS");var subQ11=sQuery(id+"F11.wireOp",EDGE,"E15.MirrorCS");var subQ12=sQuery(id+"F11.wireOp",EDGE,"E14.right");var subQ13=sQuery(id+"F11.wireOp",EDGE,"E14.left");var subQ14=sQuery(id+"F11.wireOp",EDGE,"E14.top");var subQ15=sQuery(id+"F11.wireOp",EDGE,"E14.bottom");var subQ16=sQuery(id+"F0.wireOp",EDGE,"E2");var subQ17=sQuery(id+"F0.wireOp",EDGE,"E1");var subQ18=sQuery(id+"F0.wireOp",EDGE,"E0.right");var subQ19=sQuery(id+"F0.wireOp",EDGE,"E0.left");var subQ20=sQuery(id+"F0.wireOp",EDGE,"E0.top");var subQ21=sQuery(id+"F0.wireOp",EDGE,"E0.bottom");var subQ27=makeQuery(id+"F1.opExtrude","CAP_FACE",FACE,{"disambiguationData":[OSD([subQ21,subQ20,subQ19,subQ18,subQ17,subQ16])],"isStart":false});Q1=makeQuery(id+"F33.boolean.opBoolean","MERGE",FACE,{"derivedFrom":[makeQuery(id+"F29.boolean.opBoolean","MERGE",FACE,{"derivedFrom":[makeQuery(id+"F24.boolean.opBoolean","MERGE",FACE,{"derivedFrom":[makeQuery(id+"F12.boolean.opBoolean","MERGE",FACE,{"derivedFrom":[makeQuery(id+"F7.boolean.opBoolean","SPLIT",FACE,{"disambiguationData":[TD([makeQuery(id+"F1.opExtrude","SWEPT_FACE",FACE,{"disambiguationData":[OSD([subQ19])]})])],"derivedFrom":subQ27}),makeQuery(id+"F12.opExtrude","CAP_FACE",FACE,{"disambiguationData":[OSD([subQ11,subQ10,subQ9,subQ8])],"isStart":false})]}),makeQuery(id+"F12.boolean.opBoolean","MERGE",FACE,{"derivedFrom":[makeQuery(id+"F7.boolean.opBoolean","SPLIT",FACE,{"disambiguationData":[TD([makeQuery(id+"F1.opExtrude","SWEPT_FACE",FACE,{"disambiguationData":[OSD([subQ18])]})])],"derivedFrom":subQ27}),makeQuery(id+"F12.opExtrude","CAP_FACE",FACE,{"disambiguationData":[OSD([subQ15,subQ14,subQ13,subQ12])],"isStart":false})]}),makeQuery(id+"F24.opExtrude","CAP_FACE",FACE,{"disambiguationData":[OSD([subQ7,subQ6,subQ5,subQ4])],"isStart":false}),makeQuery(id+"F24.opExtrude","CAP_FACE",FACE,{"disambiguationData":[OSD([subQ3,subQ2,subQ1,subQ0])],"isStart":false})]}),makeQuery(id+"F29.opExtrude","CAP_FACE",FACE,{"disambiguationData":[OSD([subQ21,subQ20,subQ19,subQ18,subQ17,subQ16,subQ15,subQ14,subQ13,subQ12,subQ11,subQ10,subQ9,subQ8,subQ7,subQ6,subQ5,subQ4,subQ3,subQ2,subQ1,subQ0])],"isStart":false})]}),makeQuery(id+"F33.opExtrude","CAP_FACE",FACE,{"disambiguationData":[OSD([sQuery(id+"F32.wireOp",EDGE,"E34")])],"isStart":true}),makeQuery(id+"F33.opExtrude","CAP_FACE",FACE,{"disambiguationData":[OSD([sQuery(id+"F32.wireOp",EDGE,"E35")])],"isStart":true})]});}
            extrude(context, id + "F39", {"entities" : qUnion([Q0]), "operationType" : NewBodyOperationType.ADD, "endBound" : BoundingType.UP_TO_SURFACE, "oppositeDirection" : true, "depth" : 25 * mm, "endBoundEntityFace" : qUnion([Q1]), "offsetDistance" : 25 * mm});
        }
        {
            var Q0;
            Q0=qCreatedBy(makeId("Top.planeOp"),FACE);
            var sketch = newSketch(context, id + "F40", { "sketchPlane" : qUnion([Q0])});
            skCircle(sketch, "E47", {"center": v(0, 0) * mm, "radius": 4.5 * mm});
            skCircle(sketch, "E48", {"center": v(0, 0) * mm, "radius": 6 * mm});
            skSolve(sketch);
        }
        {
            var Q0;
            Q0 = qSketchRegion(id + "F40", true);
            extrude(context, id + "F41", {"entities" : qUnion([Q0]), "oppositeDirection" : true, "depth" : 19 * mm, "offsetDistance" : 25 * mm, "hasSecondDirection" : true, "secondDirectionOppositeDirection" : false, "secondDirectionDepth" : 8 * mm});
        }
        {
            var Q0;
            Q0=qCreatedBy(makeId("Top.planeOp"),FACE);
            var sketch = newSketch(context, id + "F42", { "sketchPlane" : qUnion([Q0])});
            skCircle(sketch, "E49", {"center": v(0, 0) * mm, "radius": 3.75 * mm});
            skCircle(sketch, "E50", {"center": v(0, 0) * mm, "radius": 6 * mm});
            skSolve(sketch);
        }
        {
            var Q0;
            Q0 = qSketchRegion(id + "F42", true);
            extrude(context, id + "F43", {"entities" : qUnion([Q0]), "operationType" : NewBodyOperationType.ADD, "endBound" : BoundingType.SYMMETRIC, "depth" : 1 * mm, "offsetDistance" : 25 * mm});
        }
        {
            var Q0;
            Q0=qCreatedBy(makeId("Right.planeOp"),FACE);
            var sketch = newSketch(context, id + "F44", { "sketchPlane" : qUnion([Q0])});
            skLineSegment(sketch, "E51.bottom", {"start": v(12.34, -0.5) * mm, "end": v(0, -0.5) * mm});
            skLineSegment(sketch, "E51.top", {"start": v(12.34, -24.82) * mm, "end": v(0, -24.82) * mm});
            skLineSegment(sketch, "E51.left", {"start": v(12.34, -0.5) * mm, "end": v(12.34, -24.82) * mm});
            skLineSegment(sketch, "E51.right", {"start": v(0, -0.5) * mm, "end": v(0, -24.82) * mm});
            skSolve(sketch);
        }
        {
            var Q0;
            Q0 = qSketchRegion(id + "F44", true);
            extrude(context, id + "F45", {"entities" : qUnion([Q0]), "operationType" : NewBodyOperationType.REMOVE, "endBound" : BoundingType.SYMMETRIC, "oppositeDirection" : true, "depth" : 25 * mm, "offsetDistance" : 25 * mm});
        }
        {
            var Q0;
            Q0=makeQuery(id+"F41.opExtrude","CAP_FACE",FACE,{"disambiguationData":[OSD([sQuery(id+"F40.wireOp",EDGE,"E47"),sQuery(id+"F40.wireOp",EDGE,"E48")])],"isStart":true});
            var sketch = newSketch(context, id + "F46", { "sketchPlane" : qUnion([Q0])});
            skLineSegment(sketch, "E52.bottom", {"start": v(0.5, 8.64) * mm, "end": v(-0.5, 8.64) * mm});
            skLineSegment(sketch, "E52.top", {"start": v(0.5, 0) * mm, "end": v(-0.5, 0) * mm});
            skLineSegment(sketch, "E52.left", {"start": v(0.5, 8.64) * mm, "end": v(0.5, 0) * mm});
            skLineSegment(sketch, "E52.right", {"start": v(-0.5, 8.64) * mm, "end": v(-0.5, 0) * mm});
            skSolve(sketch);
        }
        {
            var Q0;
            Q0 = qSketchRegion(id + "F46", true);
            extrude(context, id + "F47", {"entities" : qUnion([Q0]), "operationType" : NewBodyOperationType.REMOVE, "oppositeDirection" : true, "depth" : 25 * mm, "offsetDistance" : 25 * mm});
        }
    });
